# Revit family: C750Q
name_source: partatom
category: Generic Models
revit_build: Autodesk Revit 2018 (Build: 20170223_1515(x64)
units: mm (PartAtom-declared; Revit-internal decimal feet)

## family parameters
Always vertical = Yes
Can host rebar = No
Cut with Voids When Loaded = No
Part Type = Normal
Room Calculation Point = No
Round Connector Dimension = Use Diameter
Shared = No
Work Plane-Based = No

## types (1)
- C750Q
    CONNECTIVITY- Input Terminals- Data = USB 2.0 (Media Player, 5V/2A)
    CONNECTIVITY- Input Terminals- Digital = HDMI 2.0 x2, DP 1.2 x1
    CONNECTIVITY- Input Terminals- External Control = LAN (100Mbit), 3.5mm Mini Jack IR Remote, RS-232C
    CONNECTIVITY- Output Terminals- Audio = 3.5mm Mini Jack
    Description = NEC MultiSync Large Format Display
    ENVIRONMENTAL CONDITIONS- Operating Altitude = 3000m (9843ft)
    ENVIRONMENTAL CONDITIONS- Operating Humidity = 20-80%
    ENVIRONMENTAL CONDITIONS- Operating Temperature = 0 to 50C
    LCD MODULE- Aspect Ratio = 16:9
    LCD MODULE- Brightness = 350 cd/m²
    LCD MODULE- Color Gamut = 72% NTSC
    LCD MODULE- Contrast Ratio (Typical) = 1200:1 native, not including local dimming
    LCD MODULE- Displayable Colors = Over 1.07 Billion (10bit)
    LCD MODULE- Native Resolution = 3840 x 2160
    LCD MODULE- Orientation = Landscape and Portrait (CW Rotation)
    LCD MODULE- Panel Haze (%) = 28
    LCD MODULE- Panel Technology = IPS
    LCD MODULE- Viewable Image Size = 75"
    LCD MODULE- Viewing Angle = 178° Vert., 178° Hor. (89U/89D/89L/89R) @ CR>10
    Manufacturer = NEC Display Solutions
    Model = C750Q
    PHYSICAL SPECS- Bezel Width (L/R, T/B) = 14.8mm/14.8mm/14.8mm/14.8mm
    PHYSICAL SPECS- Net Dimensions (w/o Stand, WxHxD) = 66.2 x 37.8 x 2.8 in. (1681.2 x 959.6 x 71.1mm)
    PHYSICAL SPECS- Net Weight (w/o Stand) = 116.0lbs. / 52.6kg (TBD)
    PHYSICAL SPECS- Vesa Hole Configuration = 8x M8 x 16mm (600 x 400, 400 x 400)
    POWER CONSUMPTION- Current Rating = 4.4A @ 100V, 1.9A @ 240V
    POWER CONSUMPTION- Network Standby = 2W
    POWER CONSUMPTION- Normal Standby = <0.5W
    POWER CONSUMPTION- On (Typ/Max Bightness/Overall Max) = 195W/250W/375W (TBD)
    POWER CONSUMPTION- Speaker Rating = Integrated 10W x 10W, Optional through SP-RM3a
    SENSORS- Ambient Light Sensor = Integrated
    SENSORS- Human Sensor = Optional (KT-RC3)
    SENSORS- Temperature Sensor = Integrated and programmable; linked to cooling fans
    URL = www.necdisplay.com

## geometry (parser evidence)
native form markers: Sweep x3
no freeform markers — native parametric forms only
